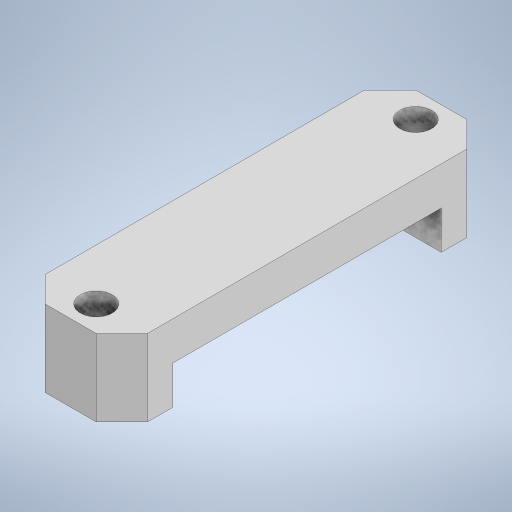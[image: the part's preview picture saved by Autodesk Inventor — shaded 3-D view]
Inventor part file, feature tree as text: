
AUTODESK INVENTOR PART (.ipt)
format: ipt  version: 2023 (Build 270158000, 158)  size: 232,960 bytes
history: native  units: mm
features: extrude x2, other x1, sketch x1, chamfer x1
ambient origin geometry x8: Origin, YZ Plane, XZ Plane, XY Plane, X Axis, Y Axis, Z Axis, Center Point
bodies: Body1 (feature_tree)
feature tree (5):
  other  "솔리드1"
  sketch  "스케치1"
  extrude  "돌출1"  Depth=8.0mm
  extrude  "돌출2"  Depth=29.0mm
  chamfer  "모따기1"  Distance=4.0mm
